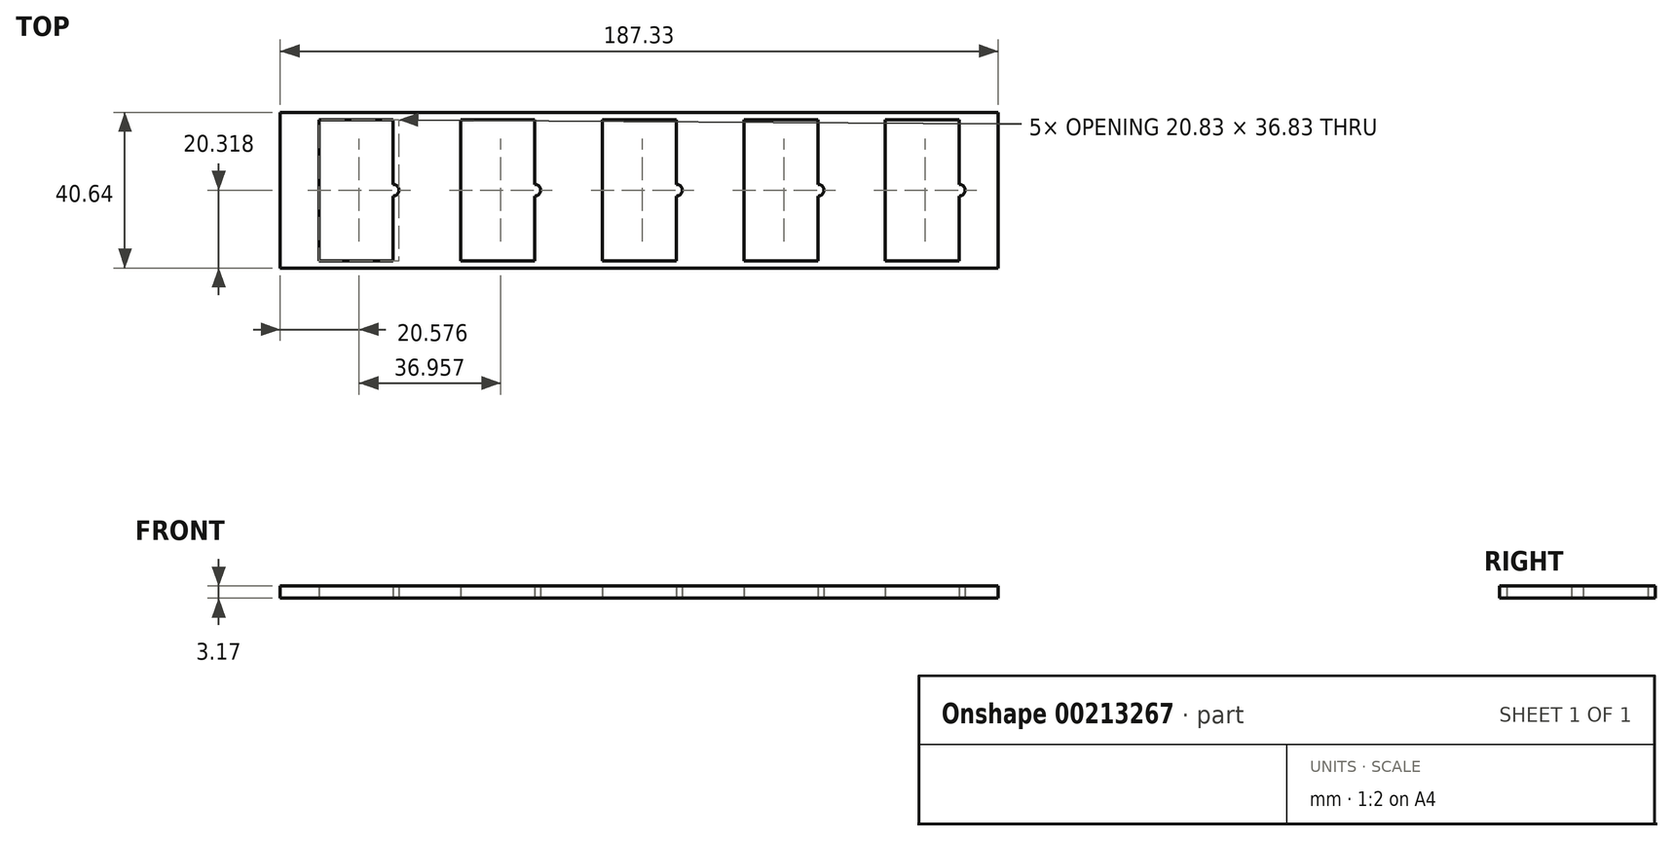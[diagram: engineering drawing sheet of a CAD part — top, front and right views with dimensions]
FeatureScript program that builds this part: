
annotation { "Feature Type Name" : "Feature", "Feature Type Description" : "" }
export const myFeature = defineFeature(function(context is Context, id is Id, definition is map)
    precondition{}
    {
        {
            var Q0;
            Q0=qCreatedBy(makeId("Top.planeOp"),FACE);
            var sketch = newSketch(context, id + "F0", { "sketchPlane" : qUnion([Q0])});
            skLineSegment(sketch, "E0.bottom", {"start": v(-43.58, 17.93) * mm, "end": v(143.75, 17.93) * mm});
            skLineSegment(sketch, "E0.top", {"start": v(-43.58, -22.71) * mm, "end": v(143.75, -22.71) * mm});
            skLineSegment(sketch, "E0.left", {"start": v(-43.58, 17.93) * mm, "end": v(-43.58, -22.71) * mm});
            skLineSegment(sketch, "E0.right", {"start": v(143.75, 17.93) * mm, "end": v(143.75, -22.71) * mm});
            skLineSegment(sketch, "E1.bottom", {"start": v(-33.42, 16.02) * mm, "end": v(-14.11, 16.02) * mm});
            skLineSegment(sketch, "E1.top", {"start": v(-33.42, -20.8) * mm, "end": v(-14.11, -20.8) * mm});
            skLineSegment(sketch, "E1.left", {"start": v(-33.42, 16.02) * mm, "end": v(-33.42, -20.8) * mm});
            skLineSegment(sketch, "E1.right", {"start": v(-14.11, 16.02) * mm, "end": v(-14.11, -20.8) * mm});
            skLineSegment(sketch, "E2.bottom", {"start": v(3.54, 16.02) * mm, "end": v(22.84, 16.02) * mm});
            skLineSegment(sketch, "E2.top", {"start": v(3.54, -20.8) * mm, "end": v(22.84, -20.8) * mm});
            skLineSegment(sketch, "E2.left", {"start": v(22.84, 16.02) * mm, "end": v(22.84, -20.8) * mm});
            skLineSegment(sketch, "E2.right", {"start": v(3.54, 16.02) * mm, "end": v(3.54, -20.8) * mm});
            skLineSegment(sketch, "E3.bottom", {"start": v(40.5, 16.02) * mm, "end": v(59.8, 16.02) * mm});
            skLineSegment(sketch, "E3.top", {"start": v(40.5, -20.8) * mm, "end": v(59.8, -20.8) * mm});
            skLineSegment(sketch, "E3.left", {"start": v(40.5, 16.02) * mm, "end": v(40.5, -20.8) * mm});
            skLineSegment(sketch, "E3.right", {"start": v(59.8, 16.02) * mm, "end": v(59.8, -20.8) * mm});
            skLineSegment(sketch, "E4.bottom", {"start": v(77.45, 16.02) * mm, "end": v(96.76, 16.02) * mm});
            skLineSegment(sketch, "E4.top", {"start": v(77.45, -20.8) * mm, "end": v(96.76, -20.8) * mm});
            skLineSegment(sketch, "E4.left", {"start": v(77.45, 16.02) * mm, "end": v(77.45, -20.8) * mm});
            skLineSegment(sketch, "E4.right", {"start": v(96.76, 16.02) * mm, "end": v(96.76, -20.8) * mm});
            skLineSegment(sketch, "E5.bottom", {"start": v(114.28, 16.02) * mm, "end": v(133.59, 16.02) * mm});
            skLineSegment(sketch, "E5.top", {"start": v(114.28, -20.8) * mm, "end": v(133.59, -20.8) * mm});
            skLineSegment(sketch, "E5.left", {"start": v(114.28, 16.02) * mm, "end": v(114.28, -20.8) * mm});
            skLineSegment(sketch, "E5.right", {"start": v(133.59, 16.02) * mm, "end": v(133.59, -20.8) * mm});
            skSolve(sketch);
        }
        {
            var Q0;
            Q0=makeQuery(id+"F0.imprint","IMPRINT",FACE,{"disambiguationData":[TD([[makeQuery(id+"F0.imprint","IMPRINT",EDGE,{"derivedFrom":sQuery(id+"F0.wireOp",EDGE,"E0.bottom")}),-1.0]])]});
            extrude(context, id + "F1", {"entities" : qUnion([Q0]), "depth" : 3.17 * mm});
        }
        {
            var Q0;
            Q0=makeQuery(id+"F1.opExtrude","CAP_FACE",FACE,{"disambiguationData":[OSD([sQuery(id+"F0.wireOp",EDGE,"E0.bottom"),sQuery(id+"F0.wireOp",EDGE,"E0.top"),sQuery(id+"F0.wireOp",EDGE,"E0.left"),sQuery(id+"F0.wireOp",EDGE,"E0.right"),sQuery(id+"F0.wireOp",EDGE,"E1.bottom"),sQuery(id+"F0.wireOp",EDGE,"E1.top"),sQuery(id+"F0.wireOp",EDGE,"E1.left"),sQuery(id+"F0.wireOp",EDGE,"E1.right"),sQuery(id+"F0.wireOp",EDGE,"E2.bottom"),sQuery(id+"F0.wireOp",EDGE,"E2.top"),sQuery(id+"F0.wireOp",EDGE,"E2.left"),sQuery(id+"F0.wireOp",EDGE,"E2.right"),sQuery(id+"F0.wireOp",EDGE,"E3.bottom"),sQuery(id+"F0.wireOp",EDGE,"E3.top"),sQuery(id+"F0.wireOp",EDGE,"E3.left"),sQuery(id+"F0.wireOp",EDGE,"E3.right"),sQuery(id+"F0.wireOp",EDGE,"E4.bottom"),sQuery(id+"F0.wireOp",EDGE,"E4.top"),sQuery(id+"F0.wireOp",EDGE,"E4.left"),sQuery(id+"F0.wireOp",EDGE,"E4.right"),sQuery(id+"F0.wireOp",EDGE,"E5.bottom"),sQuery(id+"F0.wireOp",EDGE,"E5.top"),sQuery(id+"F0.wireOp",EDGE,"E5.left"),sQuery(id+"F0.wireOp",EDGE,"E5.right")])],"isStart":false});
            var sketch = newSketch(context, id + "F2", { "sketchPlane" : qUnion([Q0])});
            skCircle(sketch, "E6", {"center": v(-14.11, -2.4) * mm, "radius": 1.52 * mm});
            skCircle(sketch, "E7", {"center": v(22.84, -2.4) * mm, "radius": 1.52 * mm});
            skCircle(sketch, "E8", {"center": v(59.8, -2.4) * mm, "radius": 1.52 * mm});
            skCircle(sketch, "E9", {"center": v(96.76, -2.4) * mm, "radius": 1.52 * mm});
            skCircle(sketch, "E10", {"center": v(133.59, -2.4) * mm, "radius": 1.52 * mm});
            skSolve(sketch);
        }
        {
            var Q0;
            Q0 = qSketchRegion(id + "F2", true);
            extrude(context, id + "F3", {"entities" : qUnion([Q0]), "operationType" : NewBodyOperationType.REMOVE, "endBound" : BoundingType.SYMMETRIC, "depth" : 12.7 * mm});
        }
    });
